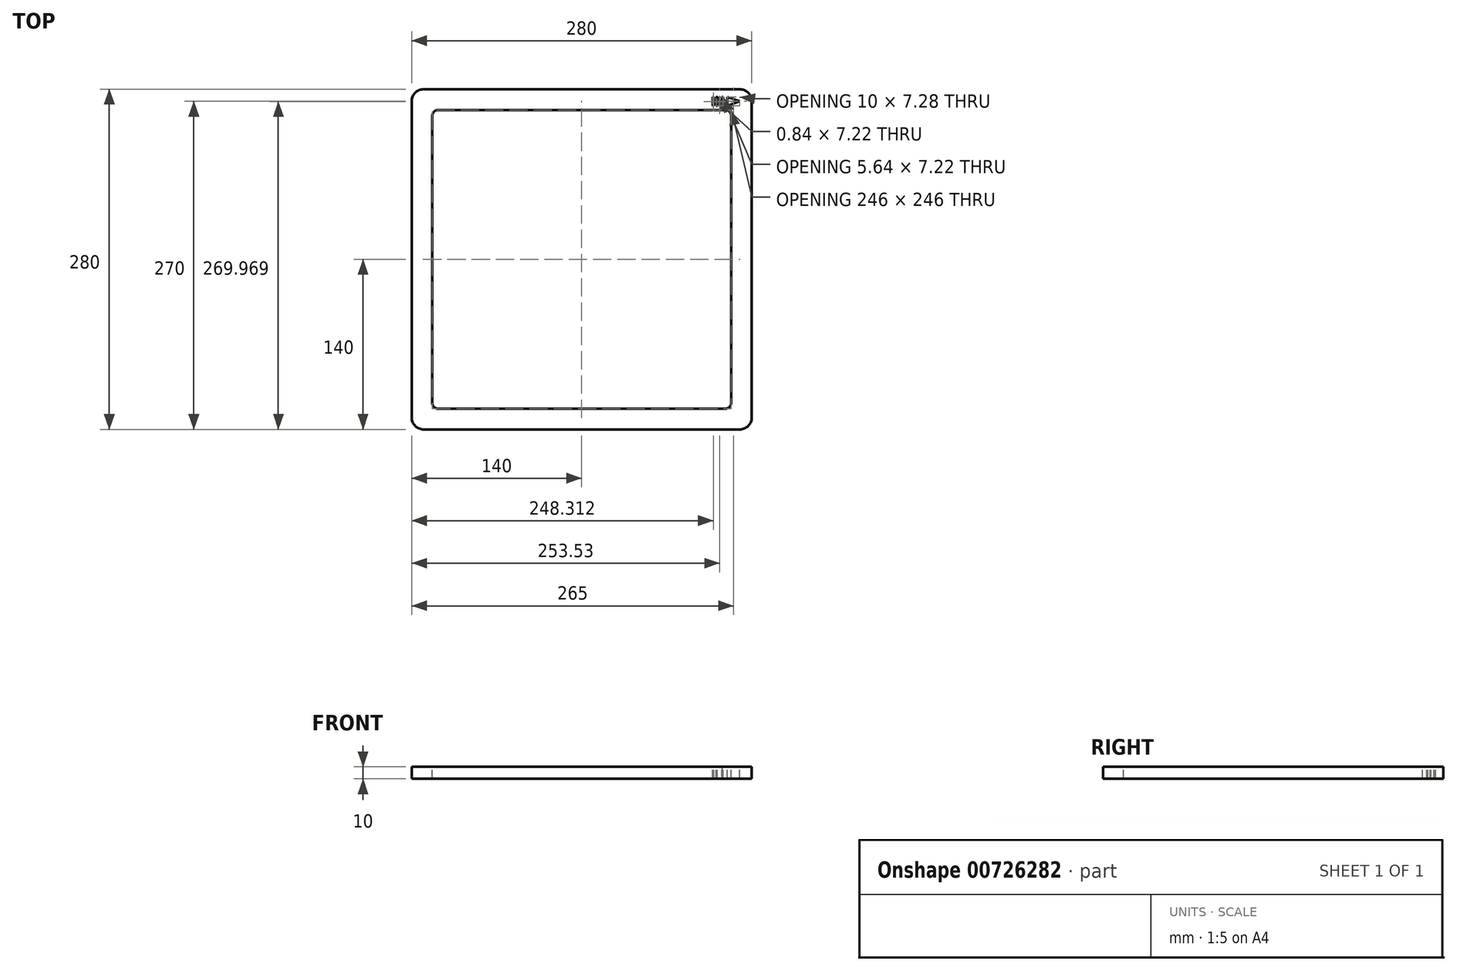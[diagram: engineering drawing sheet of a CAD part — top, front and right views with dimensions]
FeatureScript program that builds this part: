
annotation { "Feature Type Name" : "Feature", "Feature Type Description" : "" }
export const myFeature = defineFeature(function(context is Context, id is Id, definition is map)
    precondition{}
    {
        {
            var Q0;
            Q0=qCreatedBy(makeId("Top.planeOp"),FACE);
            var sketch = newSketch(context, id + "F0", { "sketchPlane" : qUnion([Q0])});
            skLineSegment(sketch, "E0.bottom", {"start": v(130, 140) * mm, "end": v(-130, 140) * mm});
            skLineSegment(sketch, "E0.top", {"start": v(130, -140) * mm, "end": v(-130, -140) * mm});
            skLineSegment(sketch, "E0.left", {"start": v(140, 130) * mm, "end": v(140, -130) * mm});
            skLineSegment(sketch, "E0.right", {"start": v(-140, 130) * mm, "end": v(-140, -130) * mm});
            skPoint(sketch, "E0.middle", {"position": v(0, 0) * mm});
            skPoint(sketch, "E1.visualSharp", {"position": v(-140, 140) * mm});
            skArc(sketch, "E1.filletArc", {"start": v(-130, 140) * mm, "mid": v(-137.07, 137.07) * mm, "end": v(-140, 130) * mm});
            skPoint(sketch, "E2.visualSharp", {"position": v(140, 140) * mm});
            skArc(sketch, "E2.filletArc", {"start": v(140, 130) * mm, "mid": v(137.07, 137.07) * mm, "end": v(130, 140) * mm});
            skPoint(sketch, "E3.visualSharp", {"position": v(140, -140) * mm});
            skArc(sketch, "E3.filletArc", {"start": v(130, -140) * mm, "mid": v(137.07, -137.07) * mm, "end": v(140, -130) * mm});
            skPoint(sketch, "E4.visualSharp", {"position": v(-140, -140) * mm});
            skArc(sketch, "E4.filletArc", {"start": v(-140, -130) * mm, "mid": v(-137.07, -137.07) * mm, "end": v(-130, -140) * mm});
            skSolve(sketch);
        }
        {
            var Q0;
            Q0 = qSketchRegion(id + "F0", true);
            extrude(context, id + "F1", {"entities" : qUnion([Q0]), "depth" : 10 * mm, "offsetDistance" : 25 * mm});
        }
        {
            var Q0;
            Q0=makeQuery(id+"F1.opExtrude","CAP_FACE",FACE,{"disambiguationData":[OSD([sQuery(id+"F0.wireOp",EDGE,"E0.bottom"),sQuery(id+"F0.wireOp",EDGE,"E0.top"),sQuery(id+"F0.wireOp",EDGE,"E0.left"),sQuery(id+"F0.wireOp",EDGE,"E0.right"),sQuery(id+"F0.wireOp",EDGE,"E1.filletArc"),sQuery(id+"F0.wireOp",EDGE,"E2.filletArc"),sQuery(id+"F0.wireOp",EDGE,"E3.filletArc"),sQuery(id+"F0.wireOp",EDGE,"E4.filletArc")])],"isStart":false});
            var sketch = newSketch(context, id + "F2", { "sketchPlane" : qUnion([Q0])});
            skLineSegment(sketch, "E5", {"start": v(-104.3, -132.15) * mm, "end": v(-104.3, 0) * mm, "construction": true});
            skLineSegment(sketch, "E6", {"start": v(-104.3, 0) * mm, "end": v(-104.3, 132.15) * mm, "construction": true});
            skLineSegment(sketch, "E7.bottom", {"start": v(-104.3, -135.15) * mm, "end": v(-104.3, -135.15) * mm});
            skLineSegment(sketch, "E7.top", {"start": v(-104.3, -129.15) * mm, "end": v(-104.3, -129.15) * mm});
            skLineSegment(sketch, "E7.left", {"start": v(-102.2, -133.05) * mm, "end": v(-102.2, -131.25) * mm});
            skLineSegment(sketch, "E7.right", {"start": v(-106.4, -133.05) * mm, "end": v(-106.4, -131.25) * mm});
            skPoint(sketch, "E7.middle", {"position": v(-104.3, -132.15) * mm});
            skPoint(sketch, "E8.visualSharp", {"position": v(-102.2, -129.15) * mm});
            skArc(sketch, "E8.filletArc", {"start": v(-102.2, -131.25) * mm, "mid": v(-102.82, -129.77) * mm, "end": v(-104.3, -129.15) * mm});
            skPoint(sketch, "E9.visualSharp", {"position": v(-106.4, -129.15) * mm});
            skArc(sketch, "E9.filletArc", {"start": v(-104.3, -129.15) * mm, "mid": v(-105.78, -129.77) * mm, "end": v(-106.4, -131.25) * mm});
            skPoint(sketch, "E10.visualSharp", {"position": v(-106.4, -135.15) * mm});
            skArc(sketch, "E10.filletArc", {"start": v(-106.4, -133.05) * mm, "mid": v(-105.78, -134.53) * mm, "end": v(-104.3, -135.15) * mm});
            skPoint(sketch, "E11.visualSharp", {"position": v(-102.2, -135.15) * mm});
            skArc(sketch, "E11.filletArc", {"start": v(-104.3, -135.15) * mm, "mid": v(-102.82, -134.53) * mm, "end": v(-102.2, -133.05) * mm});
            skCircle(sketch, "E12", {"center": v(-104.3, 132.15) * mm, "radius": 2.1 * mm});
            skCircle(sketch, "E13", {"center": v(135, 124.35) * mm, "radius": 4 * mm});
            skSolve(sketch);
        }
        {
            var Q0;
            Q0=makeQuery(id+"F1.opExtrude","CAP_FACE",FACE,{"disambiguationData":[OSD([sQuery(id+"F0.wireOp",EDGE,"E0.bottom"),sQuery(id+"F0.wireOp",EDGE,"E0.top"),sQuery(id+"F0.wireOp",EDGE,"E0.left"),sQuery(id+"F0.wireOp",EDGE,"E0.right"),sQuery(id+"F0.wireOp",EDGE,"E1.filletArc"),sQuery(id+"F0.wireOp",EDGE,"E2.filletArc"),sQuery(id+"F0.wireOp",EDGE,"E3.filletArc"),sQuery(id+"F0.wireOp",EDGE,"E4.filletArc")])],"isStart":false});
            var sketch = newSketch(context, id + "F3", { "sketchPlane" : qUnion([Q0])});
            skLineSegment(sketch, "E14", {"start": v(130, 130) * mm, "end": v(120, 133.64) * mm});
            skLineSegment(sketch, "E15", {"start": v(120, 133.64) * mm, "end": v(120, 126.36) * mm});
            skLineSegment(sketch, "E16", {"start": v(120, 126.36) * mm, "end": v(130, 130) * mm});
            skLineSegment(sketch, "E17", {"start": v(130, 130) * mm, "end": v(120, 130) * mm, "construction": true});
            skText(sketch, "E18", { "text": "IN", "fontName": "OpenSans-Regular.ttf"});
            skLineSegment(sketch, "E19.bottom", {"start": v(-118, 123) * mm, "end": v(118, 123) * mm});
            skLineSegment(sketch, "E19.top", {"start": v(-118, -123) * mm, "end": v(118, -123) * mm});
            skLineSegment(sketch, "E19.left", {"start": v(-123, 118) * mm, "end": v(-123, -118) * mm});
            skLineSegment(sketch, "E19.right", {"start": v(123, 118) * mm, "end": v(123, -118) * mm});
            skPoint(sketch, "E19.middle", {"position": v(0, 0) * mm});
            skPoint(sketch, "E20.visualSharp", {"position": v(-123, 123) * mm});
            skArc(sketch, "E20.filletArc", {"start": v(-118, 123) * mm, "mid": v(-121.54, 121.54) * mm, "end": v(-123, 118) * mm});
            skPoint(sketch, "E21.visualSharp", {"position": v(123, 123) * mm});
            skArc(sketch, "E21.filletArc", {"start": v(123, 118) * mm, "mid": v(121.54, 121.54) * mm, "end": v(118, 123) * mm});
            skPoint(sketch, "E22.visualSharp", {"position": v(123, -123) * mm});
            skArc(sketch, "E22.filletArc", {"start": v(118, -123) * mm, "mid": v(121.54, -121.54) * mm, "end": v(123, -118) * mm});
            skPoint(sketch, "E23.visualSharp", {"position": v(-123, -123) * mm});
            skArc(sketch, "E23.filletArc", {"start": v(-123, -118) * mm, "mid": v(-121.54, -121.54) * mm, "end": v(-118, -123) * mm});
            const initialGuessF3  = {"E18": [0.1069, 0.12636, 1, 0, 0.00728]};
            skSetInitialGuess(sketch, initialGuessF3);
            skSolve(sketch);
        }
        {
            var Q0;
            Q0 = qSketchRegion(id + "F3", true);
            var Q1;
            Q1=makeQuery(id+"F1.opExtrude","CAP_FACE",FACE,{"disambiguationData":[OSD([sQuery(id+"F0.wireOp",EDGE,"E0.bottom"),sQuery(id+"F0.wireOp",EDGE,"E0.top"),sQuery(id+"F0.wireOp",EDGE,"E0.left"),sQuery(id+"F0.wireOp",EDGE,"E0.right"),sQuery(id+"F0.wireOp",EDGE,"E1.filletArc"),sQuery(id+"F0.wireOp",EDGE,"E2.filletArc"),sQuery(id+"F0.wireOp",EDGE,"E3.filletArc"),sQuery(id+"F0.wireOp",EDGE,"E4.filletArc")])],"isStart":true});
            extrude(context, id + "F4", {"entities" : qUnion([Q0, Q1]), "operationType" : NewBodyOperationType.REMOVE, "endBound" : BoundingType.THROUGH_ALL, "oppositeDirection" : true, "depth" : .1 * mm, "offsetDistance" : 25 * mm});
        }
    });
